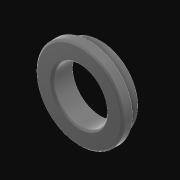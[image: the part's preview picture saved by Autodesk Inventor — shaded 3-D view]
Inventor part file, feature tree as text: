
AUTODESK INVENTOR PART (.ipt)
format: ipt  version: 2021 (Build 250183000, 183)  size: 201,216 bytes
history: native  units: in
note: dims shown in document units (in); Inventor stores cm internally (conversion verified against a paired STEP export)
features: fillet x1
ambient origin geometry x8: Origin, YZ Plane, XZ Plane, XY Plane, X Axis, Y Axis, Z Axis, Center Point
bodies: Solid1 (feature_tree)
feature tree (1):
  fillet  "Fillet1"  [1 undecoded]
note: 1 required parameter value undecoded (feature->parameter linkage not recoverable at this tier; creation-order binding heuristic only, values carry confidence <= 0.55)
